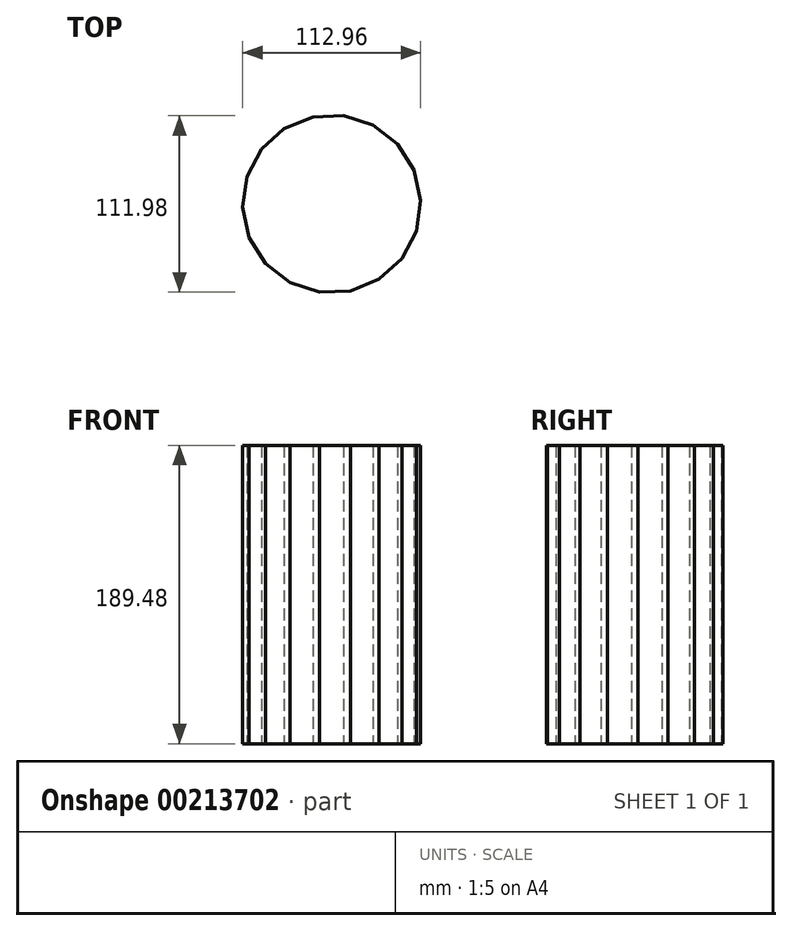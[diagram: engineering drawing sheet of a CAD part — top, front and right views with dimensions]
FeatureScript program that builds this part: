
annotation { "Feature Type Name" : "Feature", "Feature Type Description" : "" }
export const myFeature = defineFeature(function(context is Context, id is Id, definition is map)
    precondition{}
    {
        {
            var Q0;
            Q0=qCreatedBy(makeId("Top.planeOp"),FACE);
            var sketch = newSketch(context, id + "F0", { "sketchPlane" : qUnion([Q0])});
            skCircle(sketch, "E0.cCircle", {"center": v(0, 0) * mm, "radius": 55.66 * mm, "construction": true});
            skLineSegment(sketch, "E0.0", {"start": v(41.89, 37.95) * mm, "end": v(52.34, 21.33) * mm});
            skLineSegment(sketch, "E0.1", {"start": v(52.34, 21.33) * mm, "end": v(56.48, 2.14) * mm});
            skLineSegment(sketch, "E0.2", {"start": v(56.48, 2.14) * mm, "end": v(53.8, -17.3) * mm});
            skLineSegment(sketch, "E0.3", {"start": v(53.8, -17.3) * mm, "end": v(44.64, -34.66) * mm});
            skLineSegment(sketch, "E0.4", {"start": v(44.64, -34.66) * mm, "end": v(30.1, -47.84) * mm});
            skLineSegment(sketch, "E0.5", {"start": v(30.1, -47.84) * mm, "end": v(11.92, -55.25) * mm});
            skLineSegment(sketch, "E0.6", {"start": v(11.92, -55.25) * mm, "end": v(-7.7, -56) * mm});
            skLineSegment(sketch, "E0.7", {"start": v(-7.7, -56) * mm, "end": v(-26.39, -49.98) * mm});
            skLineSegment(sketch, "E0.8", {"start": v(-26.39, -49.98) * mm, "end": v(-41.89, -37.95) * mm});
            skLineSegment(sketch, "E0.9", {"start": v(-41.89, -37.95) * mm, "end": v(-52.34, -21.33) * mm});
            skLineSegment(sketch, "E0.10", {"start": v(-52.34, -21.33) * mm, "end": v(-56.48, -2.14) * mm});
            skLineSegment(sketch, "E0.11", {"start": v(-56.48, -2.14) * mm, "end": v(-53.8, 17.3) * mm});
            skLineSegment(sketch, "E0.12", {"start": v(-53.8, 17.3) * mm, "end": v(-44.64, 34.66) * mm});
            skLineSegment(sketch, "E0.13", {"start": v(-44.64, 34.66) * mm, "end": v(-30.1, 47.84) * mm});
            skLineSegment(sketch, "E0.14", {"start": v(-30.1, 47.84) * mm, "end": v(-11.92, 55.25) * mm});
            skLineSegment(sketch, "E0.15", {"start": v(-11.92, 55.25) * mm, "end": v(7.7, 56) * mm});
            skLineSegment(sketch, "E0.16", {"start": v(7.7, 56) * mm, "end": v(26.39, 49.98) * mm});
            skLineSegment(sketch, "E0.17", {"start": v(26.39, 49.98) * mm, "end": v(41.89, 37.95) * mm});
            skPoint(sketch, "E0.0.midPoint", {"position": v(47.12, 29.64) * mm});
            skSolve(sketch);
        }
        {
            var Q0;
            Q0=makeQuery(id+"F0.imprint","IMPRINT",FACE,{"disambiguationData":[TD([[makeQuery(id+"F0.imprint","IMPRINT",EDGE,{"derivedFrom":sQuery(id+"F0.wireOp",EDGE,"E0.0")}),-1.0]])]});
            extrude(context, id + "F1", {"entities" : qUnion([Q0]), "depth" : 189.48 * mm});
        }
    });
